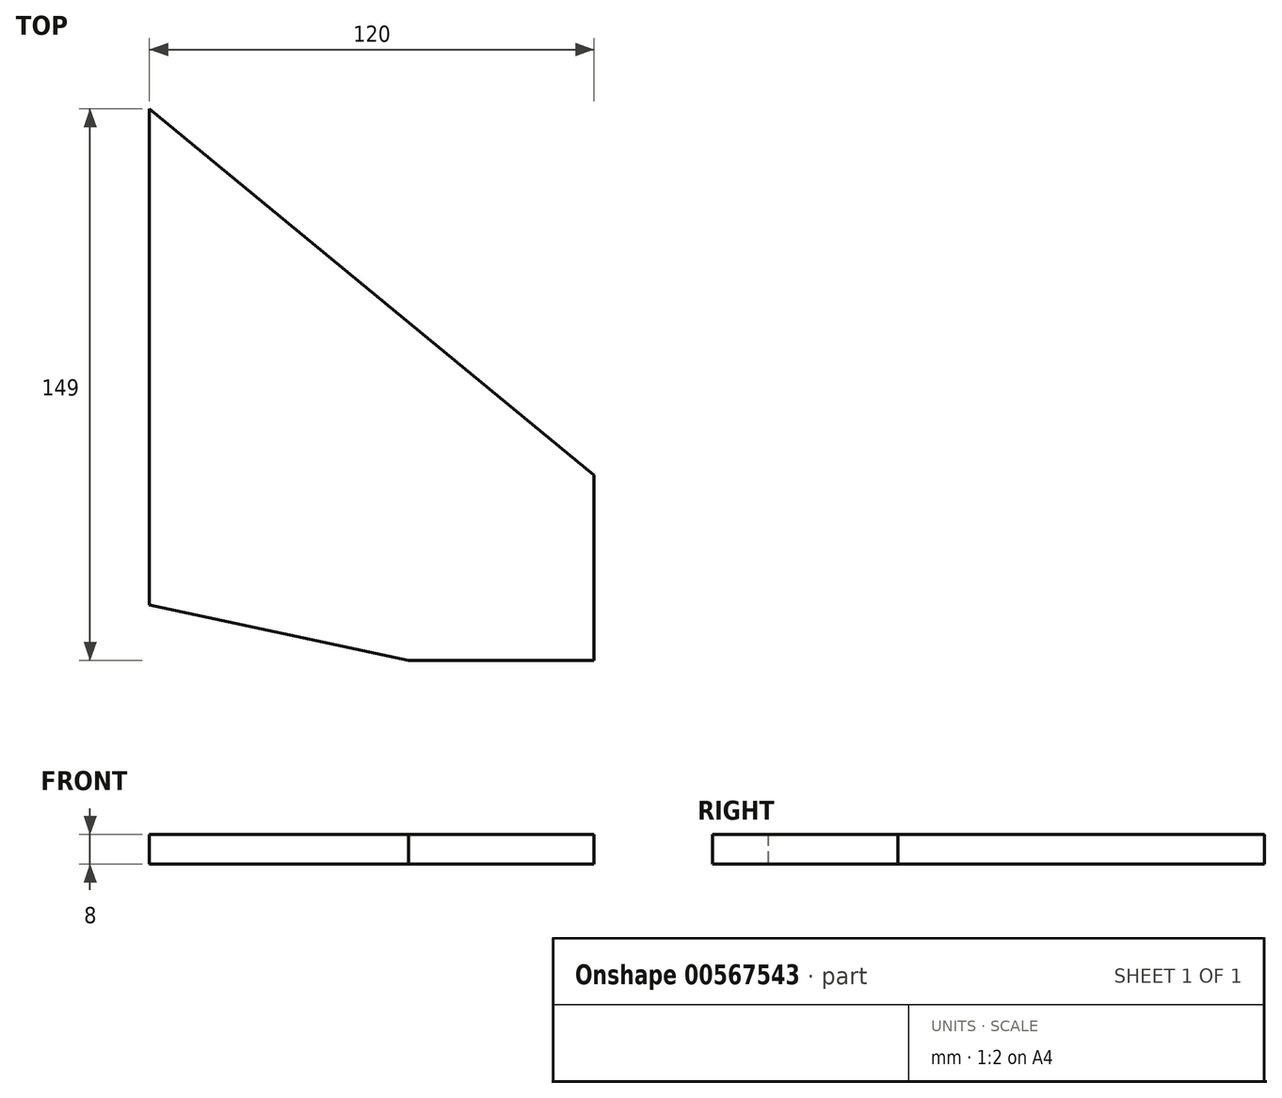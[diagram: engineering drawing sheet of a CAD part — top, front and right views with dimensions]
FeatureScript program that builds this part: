
annotation { "Feature Type Name" : "Feature", "Feature Type Description" : "" }
export const myFeature = defineFeature(function(context is Context, id is Id, definition is map)
    precondition{}
    {
        {
            var Q0;
            Q0=qCreatedBy(makeId("Top.planeOp"),FACE);
            var sketch = newSketch(context, id + "F0", { "sketchPlane" : qUnion([Q0])});
            skLineSegment(sketch, "E0", {"start": v(0, 0) * mm, "end": v(0, 134) * mm});
            skLineSegment(sketch, "E1", {"start": v(0, 134) * mm, "end": v(120, 35) * mm});
            skLineSegment(sketch, "E2", {"start": v(120, 35) * mm, "end": v(120, -15) * mm});
            skLineSegment(sketch, "E3", {"start": v(120, -15) * mm, "end": v(70, -15) * mm});
            skLineSegment(sketch, "E4", {"start": v(70, -15) * mm, "end": v(0, 0) * mm});
            skSolve(sketch);
        }
        {
            var Q0;
            Q0 = qSketchRegion(id + "F0", true);
            extrude(context, id + "F1", {"entities" : qUnion([Q0]), "depth" : 8 * mm, "offsetDistance" : 25 * mm});
        }
    });
